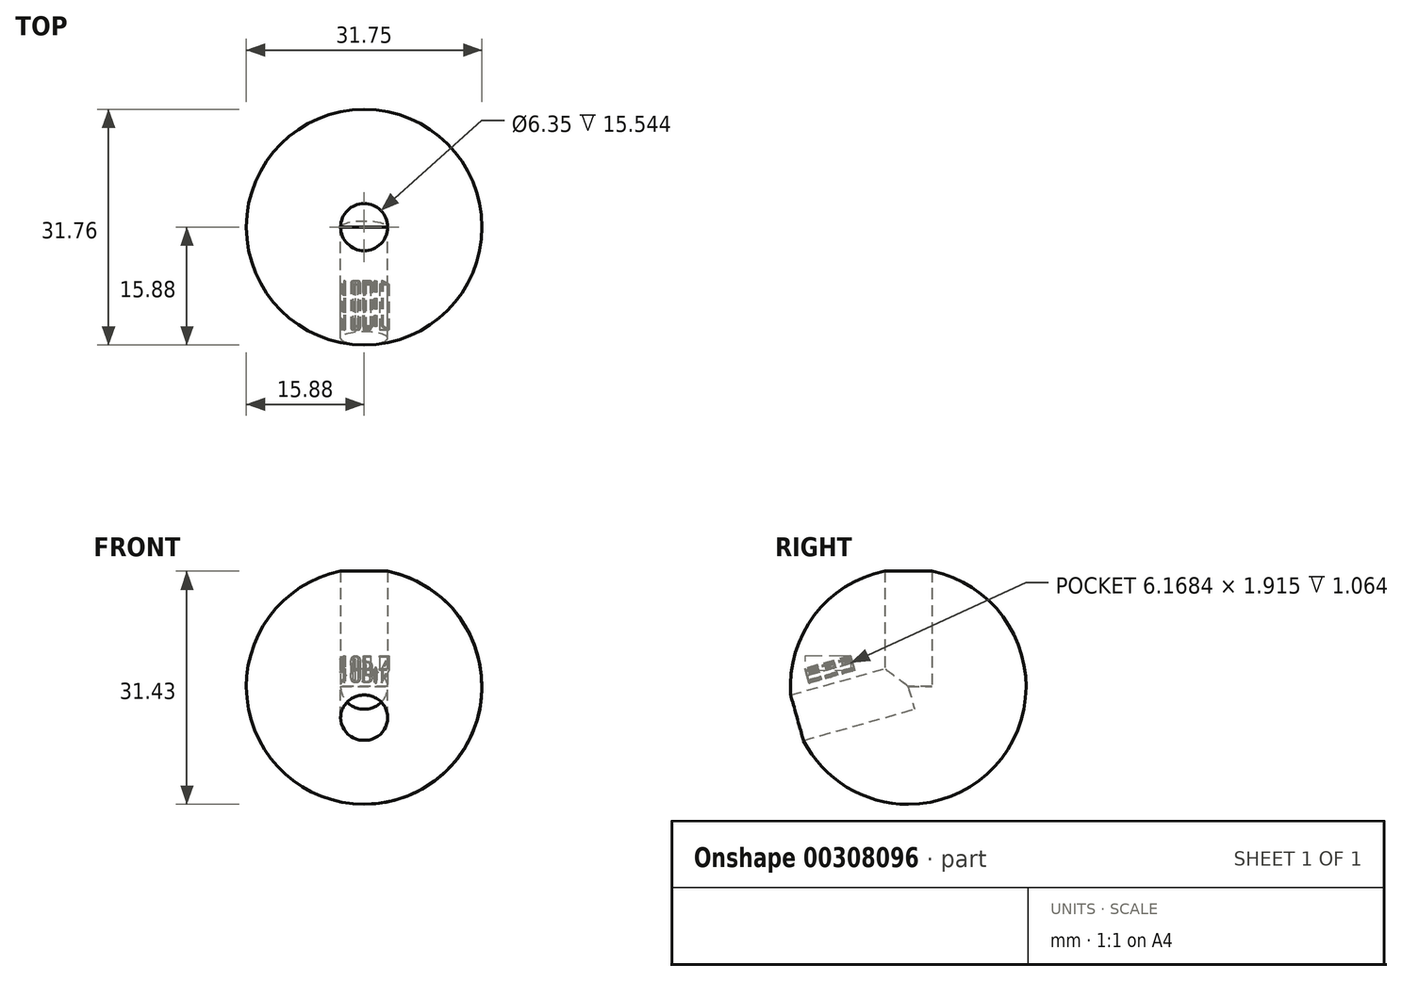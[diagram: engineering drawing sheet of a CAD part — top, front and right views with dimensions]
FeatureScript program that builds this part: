
annotation { "Feature Type Name" : "Feature", "Feature Type Description" : "" }
export const myFeature = defineFeature(function(context is Context, id is Id, definition is map)
    precondition{}
    {
        {
            var Q0;
            Q0=qCreatedBy(makeId("Front.planeOp"),FACE);
            var sketch = newSketch(context, id + "F0", { "sketchPlane" : qUnion([Q0])});
            skArc(sketch, "E0", {"start": v(0, 15.88) * mm, "mid": v(-15.88, 0) * mm, "end": v(0, -15.88) * mm});
            skLineSegment(sketch, "E1", {"start": v(0, 15.88) * mm, "end": v(0, -15.88) * mm});
            skSolve(sketch);
        }
        {
            var Q0;
            Q0=qCreatedBy(makeId("Top.planeOp"),FACE);
            var sketch = newSketch(context, id + "F1", { "sketchPlane" : qUnion([Q0])});
            skCircle(sketch, "E2", {"center": v(0, 0) * mm, "radius": 15.88 * mm});
            skSolve(sketch);
        }
        {
            var Q0;
            Q0=makeQuery(id+"F0.imprint","IMPRINT",FACE,{"disambiguationData":[TD([[makeQuery(id+"F0.imprint","IMPRINT",EDGE,{"derivedFrom":sQuery(id+"F0.wireOp",EDGE,"E0")}),1.0]])]});
            var Q1;
            Q1=sQuery(id+"F1.wireOp",EDGE,"E2");
            revolve(context, id + "F2", {"entities" : qUnion([Q0]), "axis" : qUnion([Q1]), "revolveType" : RevolveType.FULL});
        }
        {
            var Q0;
            Q0=qCreatedBy(makeId("Top.planeOp"),FACE);
            cPlane(context, id + "F3", {"entities" : qUnion([Q0]), "cplaneType" : CPlaneType.OFFSET, "offset" : 2 / 203.2 * mm, "width" : 152.4 * mm, "height" : 152.4 * mm});
        }
        {
            var Q0;
            Q0=qCreatedBy(id+"F3.planeOp",FACE);
            var sketch = newSketch(context, id + "F4", { "sketchPlane" : qUnion([Q0])});
            skCircle(sketch, "E3", {"center": v(0, 0) * mm, "radius": 3.18 * mm});
            skSolve(sketch);
        }
        {
            var Q0;
            Q0=qSketchRegion(id+"F4",true);
            extrude(context, id + "F5", {"entities" : qUnion([Q0]), "depth" : 50.8 * mm});
        }
        {
            var Q0;
            Q0=qCreatedBy(makeId("Front.planeOp"),FACE);
            var sketch = newSketch(context, id + "F6", { "sketchPlane" : qUnion([Q0])});
            skLineSegment(sketch, "E4", {"start": v(0, 0) * mm, "end": v(0, 65.12) * mm, "construction": true});
            skLineSegment(sketch, "E5", {"start": v(0, 0) * mm, "end": v(58.07, 0) * mm, "construction": true});
            skSolve(sketch);
        }
        {
            var Q0;
            Q0=makeQuery(id+"F5.opExtrude","SWEPT_BODY",BODY,{"disambiguationData":[OSD([sQuery(id+"F4.wireOp",EDGE,"E3")])]});
            var Q1;
            Q1=sQuery(id+"F6.wireOp",EDGE,"E5");
            var Q2;
            Q2=sQuery(id+"F6.wireOp",EDGE,"E5");
            transform(context, id + "F7", {"entities" : qUnion([Q0]), "transformType" : TransformType.ROTATION, "transformAxis" : qUnion([Q2]), "angle" : 105.7 * degree, "makeCopy" : true});
        }
        {
            var Q0;
            Q0=makeQuery(id+"F7.opPattern","COPY",FACE,{"derivedFrom":makeQuery(id+"F5.opExtrude","CAP_FACE",FACE,{"disambiguationData":[OSD([sQuery(id+"F4.wireOp",EDGE,"E3")])],"isStart":false}),"instanceName":"1"});
            cPlane(context, id + "F8", {"entities" : qUnion([Q0]), "cplaneType" : CPlaneType.OFFSET, "offset" : 38.1 * mm, "oppositeDirection" : true, "width" : 152.4 * mm, "height" : 152.4 * mm});
        }
        {
            var Q0;
            Q0=qCreatedBy(id+"F8.planeOp",FACE);
            var sketch = newSketch(context, id + "F9", { "sketchPlane" : qUnion([Q0])});
            skText(sketch, "E6", { "text": "105.7", "fontName": "OpenSans-Regular.ttf"});
            const initialGuessF9  = {"E6": [-0.0035, 0.00411, 1, 0, 0.00197]};
            skSetInitialGuess(sketch, initialGuessF9);
            skSolve(sketch);
        }
        {
            var Q0;
            Q0 = qSketchRegion(id + "F9", true);
            extrude(context, id + "F10", {"entities" : qUnion([Q0]), "operationType" : NewBodyOperationType.REMOVE, "oppositeDirection" : true, "depth" : 6.35 * mm});
        }
        {
            var Q0;
            Q0=makeQuery(id+"F5.opExtrude","SWEPT_BODY",BODY,{"disambiguationData":[OSD([sQuery(id+"F4.wireOp",EDGE,"E3")])]});
            var Q1;
            Q1=makeQuery(id+"F7.opPattern","COPY",BODY,{"derivedFrom":makeQuery(id+"F5.opExtrude","SWEPT_BODY",BODY,{"disambiguationData":[OSD([sQuery(id+"F4.wireOp",EDGE,"E3")])]}),"instanceName":"1"});
            var Q2;
            Q2=makeQuery(id+"F2.opRevolve","SWEPT_BODY",BODY,{"disambiguationData":[OSD([sQuery(id+"F0.wireOp",EDGE,"E0"),sQuery(id+"F0.wireOp",EDGE,"E1")])]});
            booleanBodies(context, id + "F11", {"operationType" : BooleanOperationType.SUBTRACTION, "tools" : qUnion([Q0, Q1]), "targets" : qUnion([Q2])});
        }
    });
